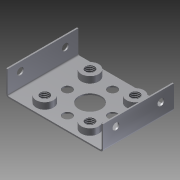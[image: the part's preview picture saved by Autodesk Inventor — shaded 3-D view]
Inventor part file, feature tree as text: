
AUTODESK INVENTOR PART (.ipt)
format: ipt  version: 2012 (Build 160160000, 160)  size: 193,024 bytes
history: native  units: mm
features: sheet_metal_op x7, sketch x7, extrude x4, thread x4, other x3
ambient origin geometry x8: Origin, YZ Plane, XZ Plane, XY Plane, X Axis, Y Axis, Z Axis, Center Point
bodies: Solid1 (feature_tree)
feature tree (25):
  sheet_metal_op  "Face1"
  sheet_metal_op  "Flange1"
  sheet_metal_op  "Flange2"
  extrude  "Extrusion1"  Depth=34.46mm
  extrude  "Extrusion2"  Depth=25.2mm
  extrude  "Extrusion3"  Depth=0.5mm
  thread  "Thread1"  [1 undecoded]
  thread  "Thread2"  [1 undecoded]
  thread  "Thread3"  [1 undecoded]
  thread  "Thread4"  [1 undecoded]
  extrude  "Extrusion4"  Depth=0.5mm
  sketch  "Sketch1"  dims[d0=17.23mm d1=34.46mm]
  other  "Plate1"
  sketch  "Sketch4"  dims[d2=12.6mm d3=25.2mm]
  other  "Plate2"
  sheet_metal_op  "Bend1"
  sheet_metal_op  "Corner1"
  sketch  "Sketch5"  dims[d4=0.5mm d6=0.5mm d7=0.25mm d8=1.0mm d9=0.5mm d10=8.75mm d11=90.0deg d12=0.5mm]
  other  "Plate3"
  sheet_metal_op  "Bend2"
  sheet_metal_op  "Corner2"
  sketch  "Sketch6"  dims[d13=2.0mm d14=0.5mm]
  sketch  "Sketch7"  dims[d15=0.5mm]
  sketch  "Sketch8"  dims[d16=0.5mm]
  sketch  "Sketch9"  dims[d17=0.25mm d18=1.0mm d19=0.5mm d20=8.75mm d21=90.0deg d22=0.5mm d23=2.0mm d24=0.5mm d25=0.5mm d26=3.3mm d27=8.0mm d29=4.56mm d30=4.56mm d31=8.04mm d32=8.04mm d33=8.04mm d34=10.0mm d35=0.0mm d36=3.2mm d37=10.0mm d38=0.0mm d39=6.2mm d40=2.28mm d41=0.0mm d42=10.0mm d43=0.0mm d44=10.0mm d45=0.0mm d46=10.0mm d47=0.0mm d48=10.0mm d49=0.0mm d50=2.4mm d51=16.0mm d52=4.63mm d53=10.0mm d54=0.0mm]
note: 4 required parameter values undecoded (feature->parameter linkage not recoverable at this tier; creation-order binding heuristic only, values carry confidence <= 0.55)
